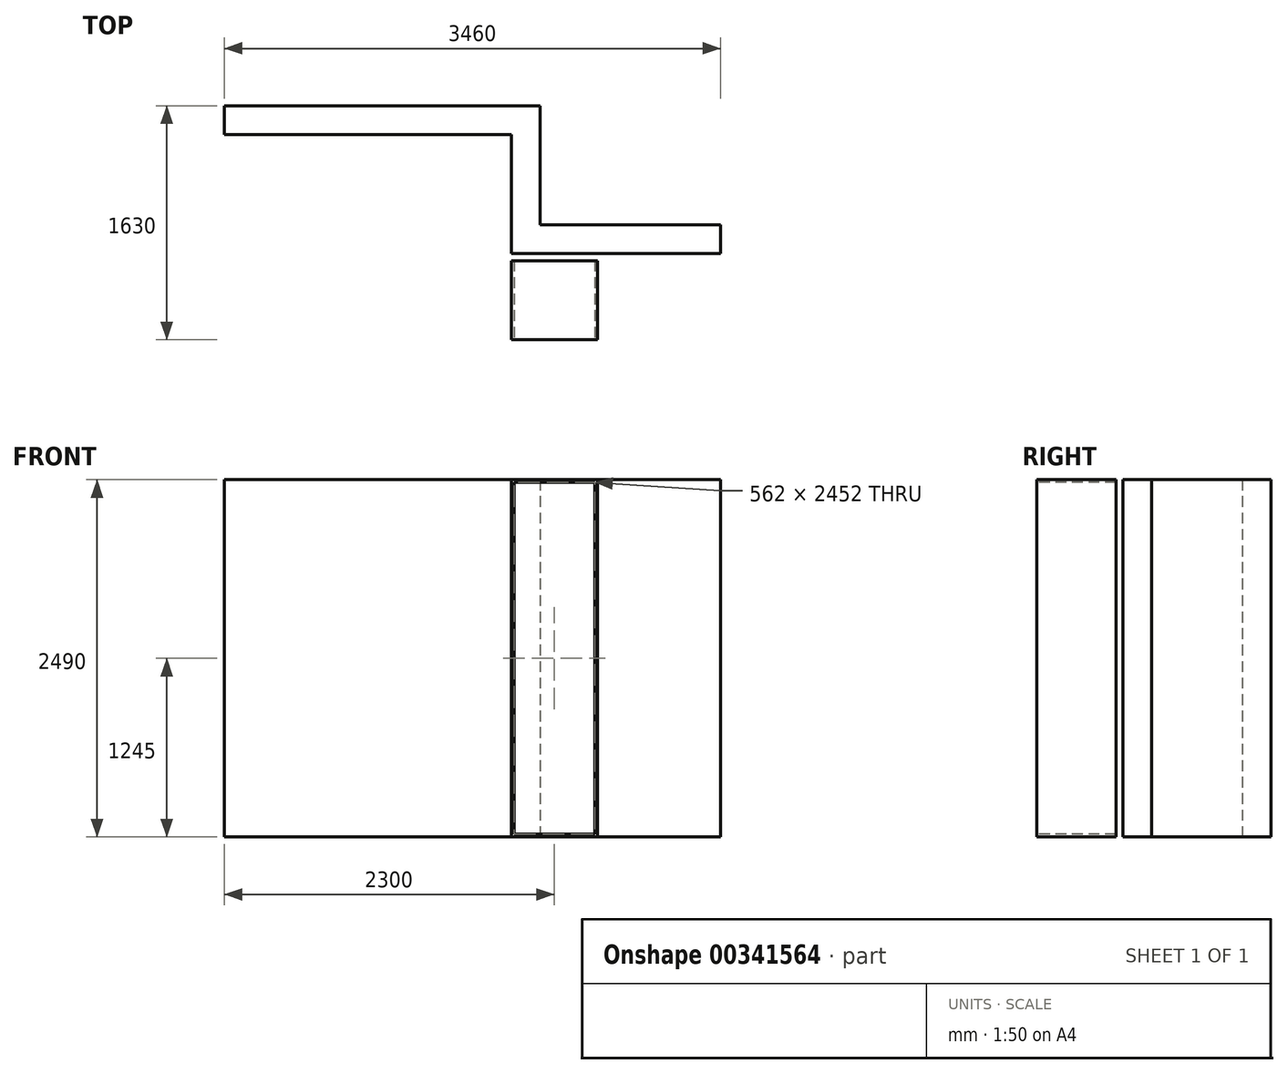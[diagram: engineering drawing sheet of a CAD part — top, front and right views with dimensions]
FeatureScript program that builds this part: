
annotation { "Feature Type Name" : "Feature", "Feature Type Description" : "" }
export const myFeature = defineFeature(function(context is Context, id is Id, definition is map)
    precondition{}
    {
        {
            var Q0;
            Q0=qCreatedBy(makeId("Top.planeOp"),FACE);
            var sketch = newSketch(context, id + "F0", { "sketchPlane" : qUnion([Q0])});
            skLineSegment(sketch, "E0.bottom", {"start": v(0, 0) * mm, "end": v(-1460, 0) * mm});
            skLineSegment(sketch, "E0.top", {"start": v(0, 200) * mm, "end": v(-1460, 200) * mm});
            skLineSegment(sketch, "E0.left", {"start": v(0, 0) * mm, "end": v(0, 200) * mm});
            skLineSegment(sketch, "E0.right", {"start": v(-1460, 0) * mm, "end": v(-1460, 200) * mm});
            skLineSegment(sketch, "E1", {"start": v(-1460, 200) * mm, "end": v(-1460, 830) * mm});
            skLineSegment(sketch, "E2", {"start": v(-1460, 830) * mm, "end": v(-3460, 830) * mm});
            skLineSegment(sketch, "E3.0", {"start": v(-1260, 1030) * mm, "end": v(-3460, 1030) * mm});
            skLineSegment(sketch, "E3.1", {"start": v(-1260, 200) * mm, "end": v(-1260, 1030) * mm});
            skLineSegment(sketch, "E4", {"start": v(-3460, 830) * mm, "end": v(-3460, 1030) * mm});
            skSolve(sketch);
        }
        {
            var Q0;
            Q0=makeQuery(id+"F0.imprint","IMPRINT",FACE,{"disambiguationData":[TD([[makeQuery(id+"F0.imprint","IMPRINT",EDGE,{"derivedFrom":sQuery(id+"F0.wireOp",EDGE,"E0.bottom")}),-1.0]])]});
            var Q1;
            {var subQ0=sQuery(id+"F0.wireOp",EDGE,"E1");Q1=makeQuery(id+"F0.imprint","IMPRINT",FACE,{"disambiguationData":[TD([[makeQuery(id+"F0.imprint","IMPRINT",EDGE,{"derivedFrom":subQ0}),-1.0]])]});}
            extrude(context, id + "F1", {"entities" : qUnion([Q0, Q1]), "depth" : 2490 * mm});
        }
        {
            var Q0;
            Q0=qCreatedBy(makeId("Top.planeOp"),FACE);
            var sketch = newSketch(context, id + "F2", { "sketchPlane" : qUnion([Q0])});
            skLineSegment(sketch, "E5.bottom", {"start": v(-1460, -600) * mm, "end": v(-860, -600) * mm});
            skLineSegment(sketch, "E5.left", {"start": v(-1460, -600) * mm, "end": v(-1460, -50) * mm});
            skLineSegment(sketch, "E5.right", {"start": v(-860, -600) * mm, "end": v(-860, -50) * mm});
            skLineSegment(sketch, "E6", {"start": v(-1460, -50) * mm, "end": v(-860, -50) * mm});
            skPoint(sketch, "E5.top.start.orphan", {"position": v(-1460, 0) * mm});
            skSolve(sketch);
        }
        {
            var Q0;
            Q0 = qSketchRegion(id + "F2", true);
            extrude(context, id + "F3", {"entities" : qUnion([Q0]), "depth" : 2490 * mm});
        }
        {
            var Q0;
            Q0=makeQuery(id+"F3.opExtrude","SWEPT_FACE",FACE,{"disambiguationData":[OSD([sQuery(id+"F2.wireOp",EDGE,"E5.bottom")])]});
            var sketch = newSketch(context, id + "F4", { "sketchPlane" : qUnion([Q0])});
            skLineSegment(sketch, "E7.0", {"start": v(-1441, 19) * mm, "end": v(-879, 19) * mm});
            skLineSegment(sketch, "E7.1", {"start": v(-1441, 2471) * mm, "end": v(-1441, 19) * mm});
            skLineSegment(sketch, "E7.2", {"start": v(-879, 2471) * mm, "end": v(-1441, 2471) * mm});
            skLineSegment(sketch, "E7.3", {"start": v(-879, 19) * mm, "end": v(-879, 2471) * mm});
            skSolve(sketch);
        }
        {
            var Q0;
            Q0=makeQuery(id+"F4.imprint","IMPRINT",FACE,{"disambiguationData":[TD([[makeQuery(id+"F4.imprint","IMPRINT",EDGE,{"derivedFrom":sQuery(id+"F4.wireOp",EDGE,"E7.0")}),1.0]])]});
            extrude(context, id + "F5", {"entities" : qUnion([Q0]), "operationType" : NewBodyOperationType.REMOVE, "endBound" : BoundingType.UP_TO_NEXT, "oppositeDirection" : true, "depth" : 530 * mm});
        }
    });
